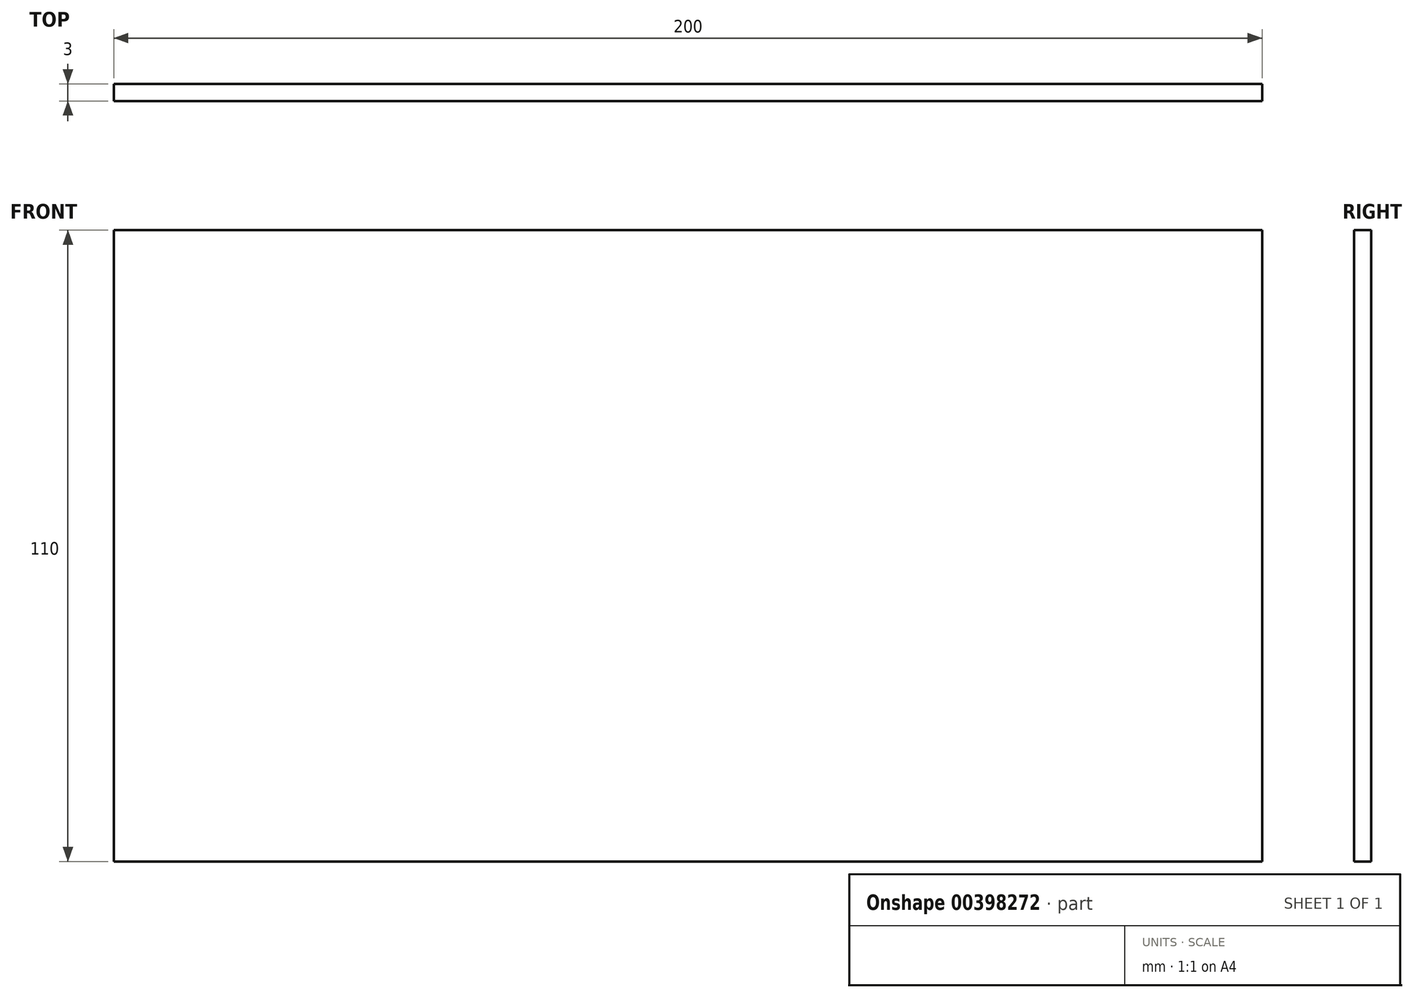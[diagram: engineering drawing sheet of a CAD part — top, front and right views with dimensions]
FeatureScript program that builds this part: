
annotation { "Feature Type Name" : "Feature", "Feature Type Description" : "" }
export const myFeature = defineFeature(function(context is Context, id is Id, definition is map)
    precondition{}
    {
        {
            var Q0;
            Q0=qCreatedBy(makeId("Front.planeOp"),FACE);
            var sketch = newSketch(context, id + "F0", { "sketchPlane" : qUnion([Q0])});
            skLineSegment(sketch, "E0.bottom", {"start": v(0, 0) * mm, "end": v(200, 0) * mm});
            skLineSegment(sketch, "E0.top", {"start": v(0, 110) * mm, "end": v(200, 110) * mm});
            skLineSegment(sketch, "E0.left", {"start": v(0, 0) * mm, "end": v(0, 110) * mm});
            skLineSegment(sketch, "E0.right", {"start": v(200, 0) * mm, "end": v(200, 110) * mm});
            skSolve(sketch);
        }
        {
            var Q0;
            Q0 = qSketchRegion(id + "F0", true);
            extrude(context, id + "F1", {"entities" : qUnion([Q0]), "depth" : 3 * mm});
        }
    });
